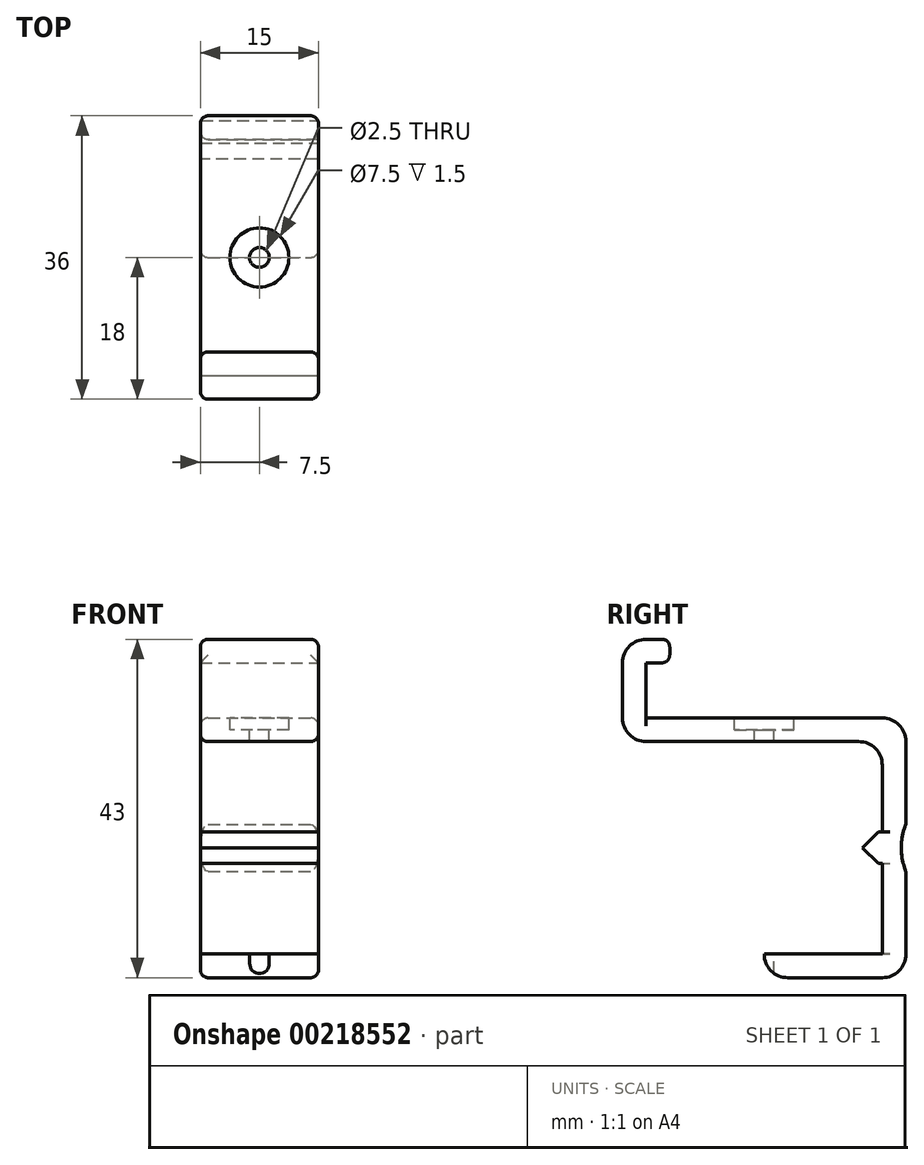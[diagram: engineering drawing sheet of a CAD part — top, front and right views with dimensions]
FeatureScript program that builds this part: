
annotation { "Feature Type Name" : "Feature", "Feature Type Description" : "" }
export const myFeature = defineFeature(function(context is Context, id is Id, definition is map)
    precondition{}
    {
        {
            var Q0;
            Q0=qCreatedBy(makeId("Top.planeOp"),FACE);
            var sketch = newSketch(context, id + "F0", { "sketchPlane" : qUnion([Q0])});
            skLineSegment(sketch, "E0.bottom", {"start": v(-7.5, 18) * mm, "end": v(7.5, 18) * mm});
            skLineSegment(sketch, "E0.top", {"start": v(-7.5, -18) * mm, "end": v(7.5, -18) * mm});
            skLineSegment(sketch, "E0.left", {"start": v(-7.5, 18) * mm, "end": v(-7.5, -18) * mm});
            skLineSegment(sketch, "E0.right", {"start": v(7.5, 18) * mm, "end": v(7.5, -18) * mm});
            skPoint(sketch, "E1", {"position": v(7.5, 0) * mm});
            skPoint(sketch, "E2", {"position": v(0, 18) * mm});
            skSolve(sketch);
        }
        {
            var Q0;
            Q0=makeQuery(id+"F0.imprint","IMPRINT",FACE,{"disambiguationData":[TD([[makeQuery(id+"F0.imprint","IMPRINT",EDGE,{"derivedFrom":sQuery(id+"F0.wireOp",EDGE,"E0.bottom")}),-1.0]])]});
            extrude(context, id + "F1", {"entities" : qUnion([Q0]), "depth" : 3 * mm});
        }
        {
            var Q0;
            Q0=makeQuery(id+"F1.opExtrude","CAP_FACE",FACE,{"disambiguationData":[OSD([sQuery(id+"F0.wireOp",EDGE,"E0.bottom"),sQuery(id+"F0.wireOp",EDGE,"E0.top"),sQuery(id+"F0.wireOp",EDGE,"E0.left"),sQuery(id+"F0.wireOp",EDGE,"E0.right")])],"isStart":false});
            var sketch = newSketch(context, id + "F2", { "sketchPlane" : qUnion([Q0])});
            skLineSegment(sketch, "E3.bottom", {"start": v(-7.5, 18) * mm, "end": v(7.5, 18) * mm});
            skLineSegment(sketch, "E3.top", {"start": v(-7.5, 15) * mm, "end": v(7.5, 15) * mm});
            skLineSegment(sketch, "E3.left", {"start": v(-7.5, 18) * mm, "end": v(-7.5, 15) * mm});
            skLineSegment(sketch, "E3.right", {"start": v(7.5, 18) * mm, "end": v(7.5, 15) * mm});
            skLineSegment(sketch, "E4.bottom", {"start": v(-7.5, -18) * mm, "end": v(7.5, -18) * mm});
            skLineSegment(sketch, "E4.top", {"start": v(-7.5, -15) * mm, "end": v(7.5, -15) * mm});
            skLineSegment(sketch, "E4.left", {"start": v(-7.5, -18) * mm, "end": v(-7.5, -15) * mm});
            skLineSegment(sketch, "E4.right", {"start": v(7.5, -18) * mm, "end": v(7.5, -15) * mm});
            skPoint(sketch, "E5", {"position": v(0, 0) * mm});
            skSolve(sketch);
        }
        {
            var Q0;
            Q0=makeQuery(id+"F2.imprint","IMPRINT",FACE,{"disambiguationData":[TD([[makeQuery(id+"F2.imprint","IMPRINT",EDGE,{"derivedFrom":sQuery(id+"F2.wireOp",EDGE,"E4.bottom")}),1.0]])]});
            extrude(context, id + "F3", {"entities" : qUnion([Q0]), "operationType" : NewBodyOperationType.ADD, "depth" : 10 * mm});
        }
        {
            var Q0;
            Q0=makeQuery(id+"F2.imprint","IMPRINT",FACE,{"disambiguationData":[TD([[makeQuery(id+"F2.imprint","IMPRINT",EDGE,{"derivedFrom":sQuery(id+"F2.wireOp",EDGE,"E3.bottom")}),-1.0]])]});
            extrude(context, id + "F4", {"entities" : qUnion([Q0]), "operationType" : NewBodyOperationType.ADD, "oppositeDirection" : true, "depth" : 33 * mm});
        }
        {
            var Q0;
            Q0=makeQuery(id+"F3.opExtrude","SWEPT_FACE",FACE,{"disambiguationData":[OSD([sQuery(id+"F2.wireOp",EDGE,"E4.top")])]});
            var sketch = newSketch(context, id + "F5", { "sketchPlane" : qUnion([Q0])});
            skLineSegment(sketch, "E6.bottom", {"start": v(7.5, 13) * mm, "end": v(-7.5, 13) * mm});
            skLineSegment(sketch, "E6.top", {"start": v(7.5, 10) * mm, "end": v(-7.5, 10) * mm});
            skLineSegment(sketch, "E6.left", {"start": v(7.5, 13) * mm, "end": v(7.5, 10) * mm});
            skLineSegment(sketch, "E6.right", {"start": v(-7.5, 13) * mm, "end": v(-7.5, 10) * mm});
            skSolve(sketch);
        }
        {
            var Q0;
            Q0=makeQuery(id+"F5.imprint","IMPRINT",FACE,{"disambiguationData":[TD([[makeQuery(id+"F5.imprint","IMPRINT",EDGE,{"derivedFrom":sQuery(id+"F5.wireOp",EDGE,"E6.bottom")}),1.0]])]});
            extrude(context, id + "F6", {"entities" : qUnion([Q0]), "operationType" : NewBodyOperationType.ADD, "depth" : 3 * mm});
        }
        {
            var Q0;
            Q0=makeQuery(id+"F4.opExtrude","SWEPT_FACE",FACE,{"disambiguationData":[OSD([sQuery(id+"F2.wireOp",EDGE,"E3.top")])]});
            var sketch = newSketch(context, id + "F7", { "sketchPlane" : qUnion([Q0])});
            skLineSegment(sketch, "E7.bottom", {"start": v(-7.5, -30) * mm, "end": v(7.5, -30) * mm});
            skLineSegment(sketch, "E7.top", {"start": v(-7.5, -27) * mm, "end": v(7.5, -27) * mm});
            skLineSegment(sketch, "E7.left", {"start": v(-7.5, -30) * mm, "end": v(-7.5, -27) * mm});
            skLineSegment(sketch, "E7.right", {"start": v(7.5, -30) * mm, "end": v(7.5, -27) * mm});
            skSolve(sketch);
        }
        {
            var Q0;
            Q0=makeQuery(id+"F7.imprint","IMPRINT",FACE,{"disambiguationData":[TD([[makeQuery(id+"F7.imprint","IMPRINT",EDGE,{"derivedFrom":sQuery(id+"F7.wireOp",EDGE,"E7.bottom")}),1.0]])]});
            extrude(context, id + "F8", {"entities" : qUnion([Q0]), "operationType" : NewBodyOperationType.ADD, "depth" : 15 * mm});
        }
        {
            var Q0;
            Q0=makeQuery(id+"F8.boolean.opBoolean","MERGE",FACE,{"derivedFrom":[makeQuery(id+"F6.boolean.opBoolean","MERGE",FACE,{"derivedFrom":[makeQuery(id+"F4.boolean.opBoolean","MERGE",FACE,{"derivedFrom":[makeQuery(id+"F3.boolean.opBoolean","MERGE",FACE,{"derivedFrom":[makeQuery(id+"F1.opExtrude","SWEPT_FACE",FACE,{"disambiguationData":[OSD([sQuery(id+"F0.wireOp",EDGE,"E0.right")])]}),makeQuery(id+"F3.opExtrude","SWEPT_FACE",FACE,{"disambiguationData":[OSD([sQuery(id+"F2.wireOp",EDGE,"E4.right")])]})]}),makeQuery(id+"F4.opExtrude","SWEPT_FACE",FACE,{"disambiguationData":[OSD([sQuery(id+"F2.wireOp",EDGE,"E3.right")])]})]}),makeQuery(id+"F6.opExtrude","SWEPT_FACE",FACE,{"disambiguationData":[OSD([sQuery(id+"F5.wireOp",EDGE,"E6.right")])]})]}),makeQuery(id+"F8.opExtrude","SWEPT_FACE",FACE,{"disambiguationData":[OSD([sQuery(id+"F7.wireOp",EDGE,"E7.right")])]})]});
            var sketch = newSketch(context, id + "F9", { "sketchPlane" : qUnion([Q0])});
            skArc(sketch, "E8", {"start": v(18, -10.5) * mm, "mid": v(17.42, -13.5) * mm, "end": v(18, -16.5) * mm});
            skSolve(sketch);
        }
        {
            var Q0;
            {var subQ0=sQuery(id+"F9.wireOp",EDGE,"E8");Q0=makeQuery(id+"F9.imprint","IMPRINT",FACE,{"disambiguationData":[TD([[makeQuery(id+"F9.imprint","IMPRINT",EDGE,{"derivedFrom":subQ0}),1.0]])]});}
            extrude(context, id + "F10", {"entities" : qUnion([Q0]), "operationType" : NewBodyOperationType.REMOVE, "endBound" : BoundingType.UP_TO_NEXT, "oppositeDirection" : true, "depth" : 25 * mm});
        }
        {
            var Q0;
            Q0=makeQuery(id+"F4.opExtrude","SWEPT_FACE",FACE,{"disambiguationData":[OSD([sQuery(id+"F2.wireOp",EDGE,"E3.top")])]});
            var sketch = newSketch(context, id + "F11", { "sketchPlane" : qUnion([Q0])});
            skLineSegment(sketch, "E9", {"start": v(-7.5, -13.5) * mm, "end": v(-7.5, -11.5) * mm});
            skLineSegment(sketch, "E10", {"start": v(-7.5, -11.5) * mm, "end": v(7.5, -11.5) * mm});
            skLineSegment(sketch, "E11", {"start": v(7.5, -11.5) * mm, "end": v(7.5, -13.5) * mm});
            skLineSegment(sketch, "E12", {"start": v(7.5, -13.5) * mm, "end": v(7.5, -15.5) * mm});
            skLineSegment(sketch, "E13", {"start": v(7.5, -15.5) * mm, "end": v(-7.5, -15.5) * mm});
            skLineSegment(sketch, "E14", {"start": v(-7.5, -15.5) * mm, "end": v(-7.5, -13.5) * mm});
            skSolve(sketch);
        }
        {
            var Q0;
            Q0=makeQuery(id+"F11.imprint","IMPRINT",FACE,{"disambiguationData":[TD([[makeQuery(id+"F11.imprint","IMPRINT",EDGE,{"derivedFrom":sQuery(id+"F11.wireOp",EDGE,"E9")}),-1.0]])]});
            extrude(context, id + "F12", {"entities" : qUnion([Q0]), "operationType" : NewBodyOperationType.ADD, "depth" : 2.5 * mm});
        }
        {
            var Q0;
            Q0=makeQuery(id+"F12.opExtrude","CAP_EDGE",EDGE,{"disambiguationData":[OSD([sQuery(id+"F11.wireOp",EDGE,"E10")])],"isStart":false});
            var Q1;
            Q1=makeQuery(id+"F12.opExtrude","CAP_EDGE",EDGE,{"disambiguationData":[OSD([sQuery(id+"F11.wireOp",EDGE,"E13")])],"isStart":false});
            chamfer(context, id + "F13", {"entities" : qUnion([Q0, Q1]), "width" : 2 * mm, "tangentPropagation" : true});
        }
        {
            var Q0;
            Q0=makeQuery(id+"F8.opExtrude","CAP_EDGE",EDGE,{"disambiguationData":[OSD([sQuery(id+"F7.wireOp",EDGE,"E7.top")])],"isStart":true});
            var Q1;
            Q1=makeQuery(id+"F4.boolean.opBoolean","INTERSECT",EDGE,{"derivedFrom":[makeQuery(id+"F1.opExtrude","CAP_FACE",FACE,{"disambiguationData":[OSD([sQuery(id+"F0.wireOp",EDGE,"E0.bottom"),sQuery(id+"F0.wireOp",EDGE,"E0.top"),sQuery(id+"F0.wireOp",EDGE,"E0.left"),sQuery(id+"F0.wireOp",EDGE,"E0.right")])],"isStart":true}),makeQuery(id+"F4.opExtrude","SWEPT_FACE",FACE,{"disambiguationData":[OSD([sQuery(id+"F2.wireOp",EDGE,"E3.top")])]})]});
            var Q2;
            Q2=makeQuery(id+"F1.opExtrude","CAP_EDGE",EDGE,{"disambiguationData":[OSD([sQuery(id+"F0.wireOp",EDGE,"E0.bottom")])],"isStart":false});
            var Q3;
            Q3=makeQuery(id+"F4.opExtrude","CAP_EDGE",EDGE,{"disambiguationData":[OSD([sQuery(id+"F2.wireOp",EDGE,"E3.bottom")])],"isStart":false});
            var Q4;
            Q4=makeQuery(id+"F8.opExtrude","CAP_EDGE",EDGE,{"disambiguationData":[OSD([sQuery(id+"F7.wireOp",EDGE,"E7.bottom")])],"isStart":false});
            var Q5;
            Q5=makeQuery(id+"F1.opExtrude","CAP_EDGE",EDGE,{"disambiguationData":[OSD([sQuery(id+"F0.wireOp",EDGE,"E0.top")])],"isStart":true});
            var Q6;
            Q6=makeQuery(id+"F3.opExtrude","CAP_EDGE",EDGE,{"disambiguationData":[OSD([sQuery(id+"F2.wireOp",EDGE,"E4.bottom")])],"isStart":false});
            fillet(context, id + "F14", {"entities" : qUnion([Q0, Q1, Q2, Q3, Q4, Q5, Q6]), "radius" : 3 * mm, "tangentPropagation" : true, "allowEdgeOverflow" : false});
        }
        {
            var Q0;
            Q0=makeQuery(id+"F3.opExtrude","CAP_EDGE",EDGE,{"disambiguationData":[OSD([sQuery(id+"F2.wireOp",EDGE,"E4.top")])],"isStart":true});
            var Q1;
            Q1=makeQuery(id+"F6.opExtrude","CAP_EDGE",EDGE,{"disambiguationData":[OSD([sQuery(id+"F5.wireOp",EDGE,"E6.top")])],"isStart":true});
            var Q2;
            Q2=makeQuery(id+"F6.opExtrude","CAP_EDGE",EDGE,{"disambiguationData":[OSD([sQuery(id+"F5.wireOp",EDGE,"E6.bottom")])],"isStart":false});
            var Q3;
            Q3=makeQuery(id+"F6.opExtrude","CAP_EDGE",EDGE,{"disambiguationData":[OSD([sQuery(id+"F5.wireOp",EDGE,"E6.top")])],"isStart":false});
            var Q4;
            Q4=makeQuery(id+"F4.boolean.opBoolean","MERGE",EDGE,{"derivedFrom":[makeQuery(id+"F1.opExtrude","SWEPT_EDGE",EDGE,{"disambiguationData":[OSD([sQuery(id+"F0.wireOp",EDGE,"E0.bottom"),sQuery(id+"F0.wireOp",EDGE,"E0.left")])]}),makeQuery(id+"F4.opExtrude","SWEPT_EDGE",EDGE,{"disambiguationData":[OSD([sQuery(id+"F2.wireOp",EDGE,"E3.bottom"),sQuery(id+"F2.wireOp",EDGE,"E3.left")])]})]});
            var Q5;
            Q5=makeQuery(id+"F1.opExtrude","CAP_EDGE",EDGE,{"disambiguationData":[OSD([sQuery(id+"F0.wireOp",EDGE,"E0.left")])],"isStart":false});
            var Q6;
            Q6=makeQuery(id+"F4.boolean.opBoolean","MERGE",EDGE,{"derivedFrom":[makeQuery(id+"F1.opExtrude","SWEPT_EDGE",EDGE,{"disambiguationData":[OSD([sQuery(id+"F0.wireOp",EDGE,"E0.bottom"),sQuery(id+"F0.wireOp",EDGE,"E0.right")])]}),makeQuery(id+"F4.opExtrude","SWEPT_EDGE",EDGE,{"disambiguationData":[OSD([sQuery(id+"F2.wireOp",EDGE,"E3.bottom"),sQuery(id+"F2.wireOp",EDGE,"E3.right")])]})]});
            var Q7;
            Q7=makeQuery(id+"F4.opExtrude","SWEPT_EDGE",EDGE,{"disambiguationData":[OSD([sQuery(id+"F0.wireOp",EDGE,"E0.left"),sQuery(id+"F2.wireOp",EDGE,"E3.top"),sQuery(id+"F2.wireOp",EDGE,"E3.left")])]});
            var Q8;
            Q8=makeQuery(id+"F1.opExtrude","CAP_EDGE",EDGE,{"disambiguationData":[OSD([sQuery(id+"F0.wireOp",EDGE,"E0.left")])],"isStart":true});
            var Q9;
            Q9=makeQuery(id+"F1.opExtrude","CAP_EDGE",EDGE,{"disambiguationData":[OSD([sQuery(id+"F0.wireOp",EDGE,"E0.right")])],"isStart":false});
            var Q10;
            Q10=makeQuery(id+"F1.opExtrude","CAP_EDGE",EDGE,{"disambiguationData":[OSD([sQuery(id+"F0.wireOp",EDGE,"E0.right")])],"isStart":true});
            var Q11;
            Q11=makeQuery(id+"F3.boolean.opBoolean","MERGE",EDGE,{"derivedFrom":[makeQuery(id+"F1.opExtrude","SWEPT_EDGE",EDGE,{"disambiguationData":[OSD([sQuery(id+"F0.wireOp",EDGE,"E0.top"),sQuery(id+"F0.wireOp",EDGE,"E0.right")])]}),makeQuery(id+"F3.opExtrude","SWEPT_EDGE",EDGE,{"disambiguationData":[OSD([sQuery(id+"F2.wireOp",EDGE,"E4.bottom"),sQuery(id+"F2.wireOp",EDGE,"E4.right")])]})]});
            var Q12;
            Q12=makeQuery(id+"F6.opExtrude","CAP_EDGE",EDGE,{"disambiguationData":[OSD([sQuery(id+"F5.wireOp",EDGE,"E6.left")])],"isStart":false});
            var Q13;
            Q13=makeQuery(id+"F6.opExtrude","CAP_EDGE",EDGE,{"disambiguationData":[OSD([sQuery(id+"F5.wireOp",EDGE,"E6.right")])],"isStart":false});
            fillet(context, id + "F15", {"entities" : qUnion([Q0, Q1, Q2, Q3, Q4, Q5, Q6, Q7, Q8, Q9, Q10, Q11, Q12, Q13]), "radius" : 1 * mm, "tangentPropagation" : true, "allowEdgeOverflow" : false});
        }
        {
            var Q0;
            Q0=sQuery(id+"F2.wireOp",VERTEX,"E5");
            var Q1;
            Q1=makeQuery(id+"F1.opExtrude","SWEPT_BODY",BODY,{"disambiguationData":[OSD([sQuery(id+"F0.wireOp",EDGE,"E0.bottom"),sQuery(id+"F0.wireOp",EDGE,"E0.top"),sQuery(id+"F0.wireOp",EDGE,"E0.left"),sQuery(id+"F0.wireOp",EDGE,"E0.right")])]});
            hole(context, id + "F16", {"style" : HoleStyle.C_BORE, "endStyle" : HoleEndStyle.THROUGH, "holeDiameter" : 2.5 * mm, "cBoreDiameter" : 7.5 * mm, "cBoreDepth" : 1.5 * mm, "startFromSketch" : true, "locations" : qUnion([Q0]), "scope" : qUnion([Q1]), "isTappedThrough" : true});
        }
    });
